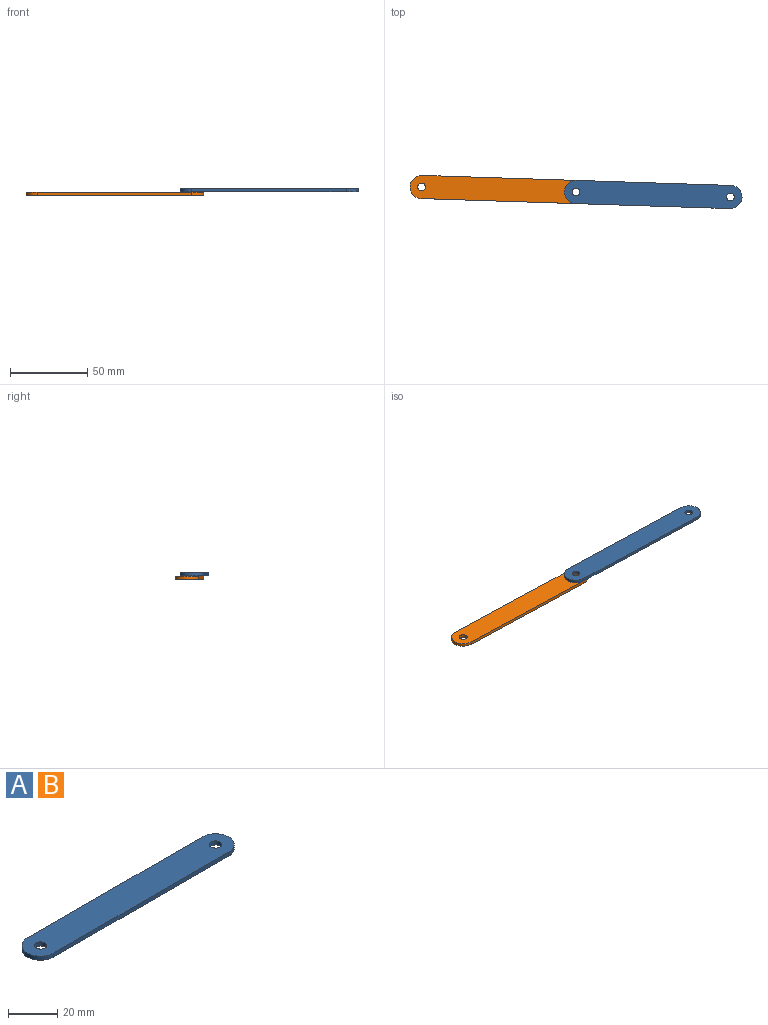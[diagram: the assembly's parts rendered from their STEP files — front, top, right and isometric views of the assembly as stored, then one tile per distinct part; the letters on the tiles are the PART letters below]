
ASSEMBLY  parts=2 mates=1
PART A: 8 faces, bbox 115x15x2 mm
  f0: plane 100x2mm, normal (0,1,0), area 200mm2, adj f1,f4,f6,f7
  f1: cylinder r=7.5mm len=15mm, axis (0,0,1), area 47.1mm2, adj f0,f2,f6,f7
  f2: plane 100x2mm, normal (0,-1,0), area 200mm2, adj f1,f4,f6,f7
  f3: cylinder r=2.5mm len=5mm, axis (0,0,1), area 31.4mm2, adj f6,f7
  f4: cylinder r=7.5mm len=15mm, axis (0,0,1), area 47.1mm2, adj f0,f2,f6,f7
  f5: cylinder r=2.5mm len=5mm, axis (0,0,1), area 31.4mm2, adj f6,f7
  f6: plane 115x15mm, normal (0,0,-1), area 1637.4mm2, adj f0,f1,f2,f3,f4,f5
  f7: plane 115x15mm, normal (0,0,1), area 1637.4mm2, adj f0,f1,f2,f3,f4,f5
PART B: same geometry as A
PLACE A rot(axis=(0,0,-1),1.9deg) t=(-64.18,-76.69,-1)mm
PLACE B rot(axis=(0,0,1),178.1deg) t=(-64.18,-76.69,-3)mm fixed
MATE revolute A.f1 <-> B.f1  axis (0,0,-1) through (-64.18,-76.69,-2)mm
